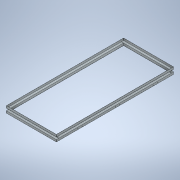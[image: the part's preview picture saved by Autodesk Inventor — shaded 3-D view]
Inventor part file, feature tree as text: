
AUTODESK INVENTOR PART (.ipt)
format: ipt  version: 2021 (Build 250183000, 183)  size: 289,792 bytes
history: native  units: mm
features: extrude x6, sketch x5, mirror x4, thicken_offset x4, other x4, projected_geometry x1
ambient origin geometry x8: Origin, YZ Plane, XZ Plane, XY Plane, X Axis, Y Axis, Z Axis, Center Point
bodies: Solid1 (feature_tree)
feature tree (24):
  mirror  "Mirror1"
  mirror  "Mirror2"
  thicken_offset  "Thicken1"
  thicken_offset  "Thicken2"
  thicken_offset  "Thicken3"
  thicken_offset  "Thicken4"
  extrude  "Extrusion1"  Depth=40.0mm
  sketch  "Sketch5"  dims[d8=920.0mm d9=0.0mm d10=1.1mm]
  extrude  "Extrusion2"  Depth=40.0mm
  mirror  "Mirror3"
  mirror  "Mirror4"
  sketch  "Sketch1"  dims[d0=40.0mm d1=40.0mm]
  other  "Srf1"
  other  "Srf2"
  sketch  "Sketch2"  dims[d2=40.0mm d3=425.0mm]
  other  "Srf3"
  other  "Srf4"
  sketch  "Sketch4"  dims[d4=40.0mm d5=2100.0mm d6=0.0mm]
  sketch  "Sketch6"  dims[d11=1.1mm d12=1.1mm d13=1.1mm d14=1.1mm d15=1.1mm d16=1.1mm d17=1.1mm d18=8.0mm d19=15.0mm d20=360.0mm d21=8.0mm d22=15.0mm d23=80.0mm d24=30.0mm d26=700.0mm d27=10.0mm d29=10.0mm d31=0.0mm d32=0.0mm d33=40.0mm d34=1050.0mm d35=40.0mm d36=20.0mm d37=40.0mm d38=40.0mm d39=840.0mm d40=0.0mm]
  projected_geometry  "Projected Loop1"
  extrude  "ExtrusionSrf1"  Depth=2100.0mm TaperAngle=0.0deg
  extrude  "ExtrusionSrf3"  Depth=1.1mm
  extrude  "ExtrusionSrf2"  Depth=1.1mm
  extrude  "ExtrusionSrf4"  Depth=1.1mm
